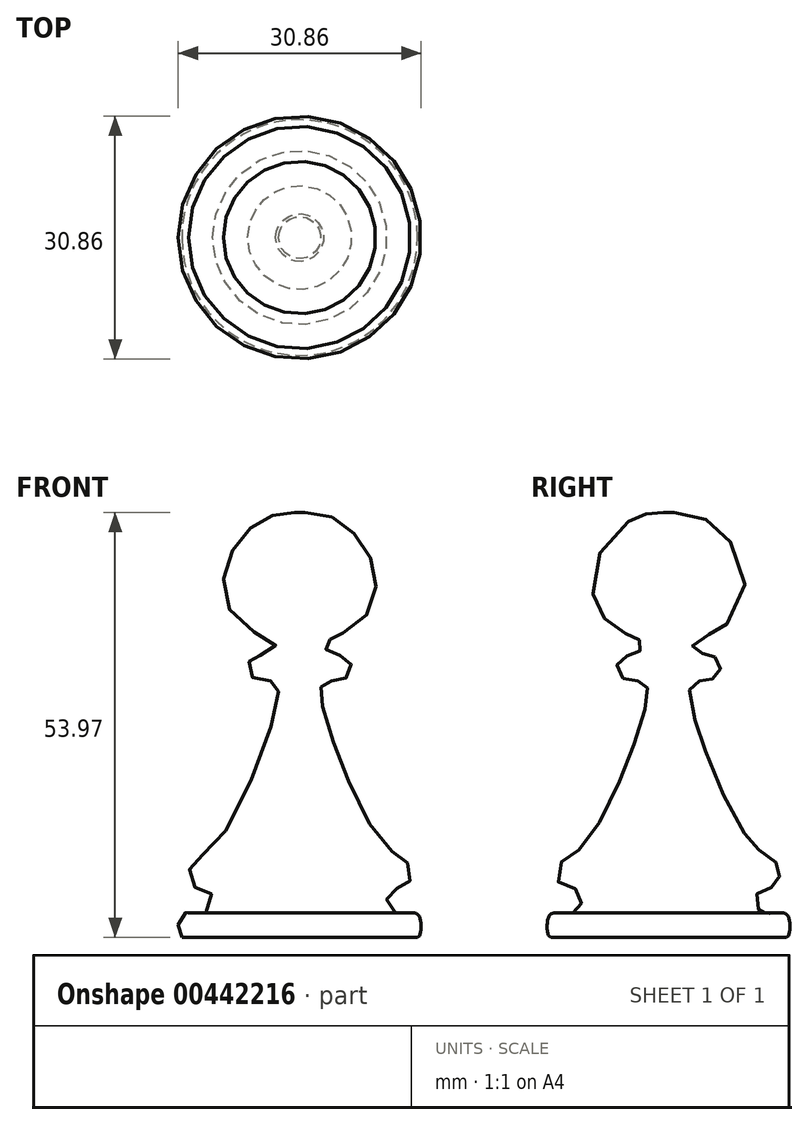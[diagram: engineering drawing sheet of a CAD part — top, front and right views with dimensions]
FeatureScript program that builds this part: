
annotation { "Feature Type Name" : "Feature", "Feature Type Description" : "" }
export const myFeature = defineFeature(function(context is Context, id is Id, definition is map)
    precondition{}
    {
        {
            var Q0;
            Q0=qCreatedBy(makeId("Front.planeOp"),FACE);
            var sketch = newSketch(context, id + "F0", { "sketchPlane" : qUnion([Q0])});
            skFitSpline(sketch, "E0", {"points": [v(0, 57.1) * mm, v(-3.35, 56.8) * mm, v(-7.12, 54.28) * mm, v(-9.63, 48.95) * mm, v(-7.43, 42.99) * mm, v(-3.04, 40.16) * mm, v(-5.24, 38.9) * mm, v(-6.18, 38.6) * mm, v(-6.5, 36.71) * mm, v(-4.6, 35.77) * mm, v(-3.04, 35.46) * mm, v(-3.04, 32) * mm, v(-10.88, 14.75) * mm, v(-13.7, 12.55) * mm, v(-13.7, 9.73) * mm, v(-11.51, 9.1) * mm, v(-11.51, 6.59) * mm, v(-14.33, 6.28) * mm, v(-15.28, 5.65) * mm, v(-15.28, 3.45) * mm, v(-14.96, 3.14) * mm], "startDerivative": vector(-64.78, 0.85) * mm, "endDerivative": vector(18.49, -9.23) * mm});
            skLineSegment(sketch, "E1", {"start": v(-14.96, 3.14) * mm, "end": v(0, 3.14) * mm});
            skLineSegment(sketch, "E2", {"start": v(0, 3.14) * mm, "end": v(0, 57.1) * mm});
            skLineSegment(sketch, "E3", {"start": v(0, 65.58) * mm, "end": v(0, -21.65) * mm});
            skPoint(sketch, "E3.endSnap0", {"position": v(0, 30.12) * mm});
            skSolve(sketch);
        }
        {
            var Q0;
            {var subQ0=sQuery(id+"F0.wireOp",EDGE,"E0");Q0=makeQuery(id+"F0.imprint","IMPRINT",FACE,{"disambiguationData":[TD([[makeQuery(id+"F0.imprint","IMPRINT",EDGE,{"derivedFrom":subQ0}),1.0]])]});}
            var Q1;
            Q1=sQuery(id+"F0.wireOp",EDGE,"E3");
            revolve(context, id + "F1", {"entities" : qUnion([Q0]), "axis" : qUnion([Q1]), "revolveType" : RevolveType.FULL});
        }
    });
